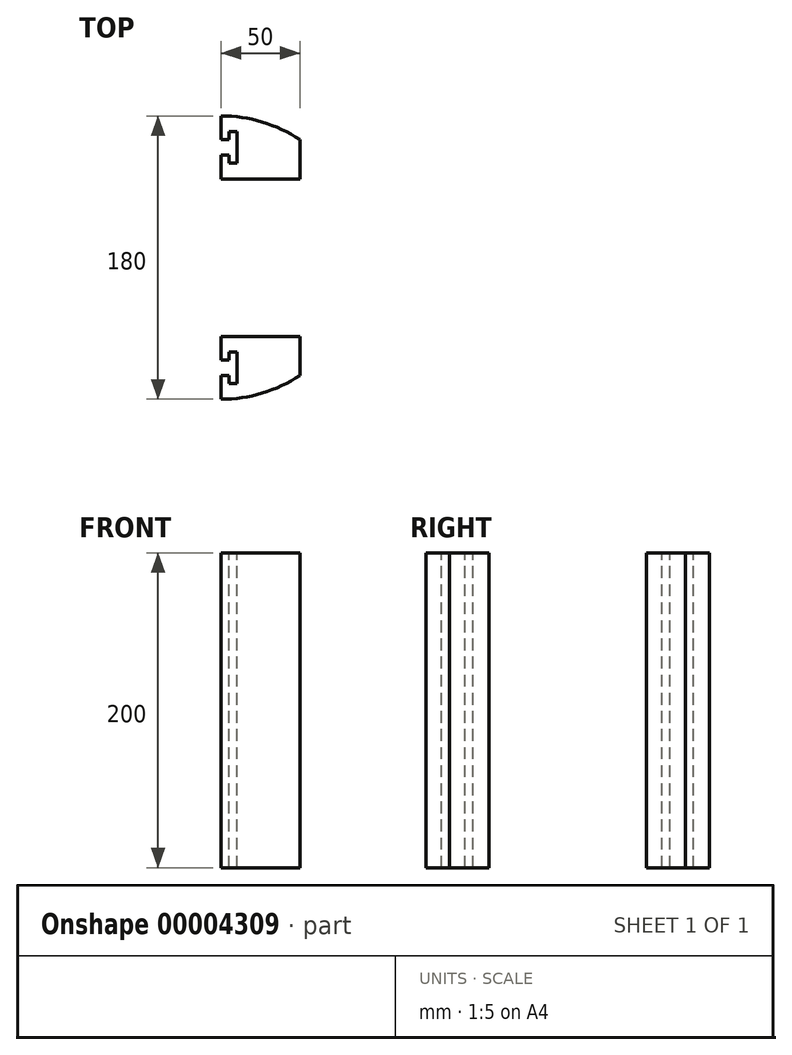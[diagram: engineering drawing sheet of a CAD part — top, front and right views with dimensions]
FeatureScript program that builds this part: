
annotation { "Feature Type Name" : "Feature", "Feature Type Description" : "" }
export const myFeature = defineFeature(function(context is Context, id is Id, definition is map)
    precondition{}
    {
        {
            var Q0;
            Q0=qCreatedBy(makeId("Top.planeOp"),FACE);
            var sketch = newSketch(context, id + "F0", { "sketchPlane" : qUnion([Q0])});
            skArc(sketch, "E0", {"start": v(0, -90) * mm, "mid": v(90, 0) * mm, "end": v(0, 90) * mm});
            skLineSegment(sketch, "E1", {"start": v(0, -90) * mm, "end": v(0, 90) * mm});
            skLineSegment(sketch, "E2.0", {"start": v(50, -90) * mm, "end": v(50, 90) * mm});
            skLineSegment(sketch, "E3", {"start": v(0, 90) * mm, "end": v(50, 90) * mm});
            skLineSegment(sketch, "E4", {"start": v(0, -90) * mm, "end": v(50, -90) * mm});
            skLineSegment(sketch, "E5.0", {"start": v(0, -50) * mm, "end": v(60, -50) * mm});
            skLineSegment(sketch, "E6.0", {"start": v(0, 50) * mm, "end": v(60, 50) * mm});
            skSolve(sketch);
        }
        {
            var Q0;
            {var subQ0=sQuery(id+"F0.wireOp",EDGE,"E6.0");Q0=makeQuery(id+"F0.imprint","IMPRINT",FACE,{"disambiguationData":[TD([[makeQuery(id+"F0.imprint","IMPRINT",EDGE,{"derivedFrom":subQ0}),1.0]])]});}
            var Q1;
            {var subQ0=sQuery(id+"F0.wireOp",EDGE,"E2.0");var subQ1=sQuery(id+"F0.wireOp",EDGE,"E0");var subQ5=makeQuery(id+"F0.imprint","INTERSECT",VERTEX,{"disambiguationData":[OD(0.0)],"derivedFrom":[subQ1,subQ0]});Q1=makeQuery(id+"F0.imprint","IMPRINT",FACE,{"disambiguationData":[TD([[makeQuery(id+"F0.imprint","IMPRINT",EDGE,{"disambiguationData":[TD([[subQ5,-1.0]])],"derivedFrom":subQ1}),1.0]])]});}
            var Q2;
            {var subQ0=sQuery(id+"F0.wireOp",EDGE,"E5.0");Q2=makeQuery(id+"F0.imprint","IMPRINT",FACE,{"disambiguationData":[TD([[makeQuery(id+"F0.imprint","IMPRINT",EDGE,{"derivedFrom":subQ0}),-1.0]])]});}
            extrude(context, id + "F1", {"entities" : qUnion([Q0, Q1, Q2]), "oppositeDirection" : true, "depth" : 200 * mm});
        }
        {
            var Q0;
            {var subQ0=sQuery(id+"F0.wireOp",EDGE,"E1");Q0=makeQuery(id+"F1.opExtrude","SWEPT_FACE",FACE,{"disambiguationData":[OSD([subQ0]),TDD([makeQuery(id+"F0.imprint","IMPRINT",EDGE,{"disambiguationData":[TD([[makeQuery(id+"F0.imprint","INTERSECT",VERTEX,{"derivedFrom":[subQ0,sQuery(id+"F0.wireOp",EDGE,"E6.0")]}),-1.0]])],"derivedFrom":subQ0})])]});}
            var sketch = newSketch(context, id + "F2", { "sketchPlane" : qUnion([Q0])});
            skLineSegment(sketch, "E7.0", {"start": v(-65, -200) * mm, "end": v(-65, 0) * mm});
            skLineSegment(sketch, "E8.0", {"start": v(-75, -200) * mm, "end": v(-75, 0) * mm});
            skLineSegment(sketch, "E9.0", {"start": v(75, -200) * mm, "end": v(75, 0) * mm});
            skLineSegment(sketch, "E10.0", {"start": v(65, -200) * mm, "end": v(65, 0) * mm});
            skLineSegment(sketch, "E11", {"start": v(65, 0) * mm, "end": v(75, 0) * mm});
            skLineSegment(sketch, "E12", {"start": v(65, -200) * mm, "end": v(75, -200) * mm});
            skSolve(sketch);
        }
        {
            var Q0;
            {var subQ4=sQuery(id+"F2.wireOp",EDGE,"E7.0");Q0=makeQuery(id+"F2.imprint","IMPRINT",FACE,{"disambiguationData":[TD([[makeQuery(id+"F2.imprint","IMPRINT",EDGE,{"derivedFrom":subQ4}),1.0]])]});}
            var Q1;
            Q1=makeQuery(id+"F2.imprint","IMPRINT",FACE,{"disambiguationData":[TD([[makeQuery(id+"F2.imprint","IMPRINT",EDGE,{"derivedFrom":sQuery(id+"F2.wireOp",EDGE,"E9.0")}),1.0]])]});
            extrude(context, id + "F3", {"entities" : qUnion([Q0, Q1]), "operationType" : NewBodyOperationType.REMOVE, "oppositeDirection" : true, "depth" : 10 * mm});
        }
        {
            var Q0;
            Q0=makeQuery(id+"F3.boolean.opBoolean","COPY",FACE,{"derivedFrom":makeQuery(id+"F3.opExtrude","SWEPT_FACE",FACE,{"disambiguationData":[OSD([sQuery(id+"F2.wireOp",EDGE,"E8.0")])]})});
            var sketch = newSketch(context, id + "F4", { "sketchPlane" : qUnion([Q0])});
            skLineSegment(sketch, "E13.0", {"start": v(5, -200) * mm, "end": v(5, 0) * mm});
            skSolve(sketch);
        }
        {
            var Q0;
            {var subQ4=sQuery(id+"F4.wireOp",EDGE,"E13.0");Q0=makeQuery(id+"F4.imprint","IMPRINT",FACE,{"disambiguationData":[TD([[makeQuery(id+"F4.imprint","IMPRINT",EDGE,{"derivedFrom":subQ4}),-1.0]])]});}
            extrude(context, id + "F5", {"entities" : qUnion([Q0]), "operationType" : NewBodyOperationType.REMOVE, "oppositeDirection" : true, "depth" : 5 * mm});
        }
        {
            var Q0;
            Q0=makeQuery(id+"F3.boolean.opBoolean","COPY",FACE,{"derivedFrom":makeQuery(id+"F3.opExtrude","SWEPT_FACE",FACE,{"disambiguationData":[OSD([sQuery(id+"F2.wireOp",EDGE,"E7.0")])]})});
            var sketch = newSketch(context, id + "F6", { "sketchPlane" : qUnion([Q0])});
            skLineSegment(sketch, "E14.0", {"start": v(-5, -200) * mm, "end": v(-5, 0) * mm});
            skSolve(sketch);
        }
        {
            var Q0;
            {var subQ4=sQuery(id+"F6.wireOp",EDGE,"E14.0");Q0=makeQuery(id+"F6.imprint","IMPRINT",FACE,{"disambiguationData":[TD([[makeQuery(id+"F6.imprint","IMPRINT",EDGE,{"derivedFrom":subQ4}),1.0]])]});}
            extrude(context, id + "F7", {"entities" : qUnion([Q0]), "operationType" : NewBodyOperationType.REMOVE, "oppositeDirection" : true, "depth" : 5 * mm});
        }
        {
            var Q0;
            Q0=makeQuery(id+"F3.boolean.opBoolean","COPY",FACE,{"derivedFrom":makeQuery(id+"F3.opExtrude","SWEPT_FACE",FACE,{"disambiguationData":[OSD([sQuery(id+"F2.wireOp",EDGE,"E10.0")])]})});
            var sketch = newSketch(context, id + "F8", { "sketchPlane" : qUnion([Q0])});
            skLineSegment(sketch, "E15.0", {"start": v(5, -200) * mm, "end": v(5, 0) * mm});
            skSolve(sketch);
        }
        {
            var Q0;
            {var subQ2=sQuery(id+"F8.wireOp",EDGE,"E15.0");Q0=makeQuery(id+"F8.imprint","IMPRINT",FACE,{"disambiguationData":[TD([[makeQuery(id+"F8.imprint","IMPRINT",EDGE,{"derivedFrom":subQ2}),-1.0]])]});}
            extrude(context, id + "F9", {"entities" : qUnion([Q0]), "operationType" : NewBodyOperationType.REMOVE, "oppositeDirection" : true, "depth" : 5 * mm});
        }
        {
            var Q0;
            Q0=makeQuery(id+"F3.boolean.opBoolean","COPY",FACE,{"derivedFrom":makeQuery(id+"F3.opExtrude","SWEPT_FACE",FACE,{"disambiguationData":[OSD([sQuery(id+"F2.wireOp",EDGE,"E9.0")])]})});
            var sketch = newSketch(context, id + "F10", { "sketchPlane" : qUnion([Q0])});
            skLineSegment(sketch, "E16.0", {"start": v(-5, -200) * mm, "end": v(-5, 0) * mm});
            skSolve(sketch);
        }
        {
            var Q0;
            {var subQ2=sQuery(id+"F10.wireOp",EDGE,"E16.0");Q0=makeQuery(id+"F10.imprint","IMPRINT",FACE,{"disambiguationData":[TD([[makeQuery(id+"F10.imprint","IMPRINT",EDGE,{"derivedFrom":subQ2}),1.0]])]});}
            extrude(context, id + "F11", {"entities" : qUnion([Q0]), "operationType" : NewBodyOperationType.REMOVE, "oppositeDirection" : true, "depth" : 5 * mm});
        }
    });
